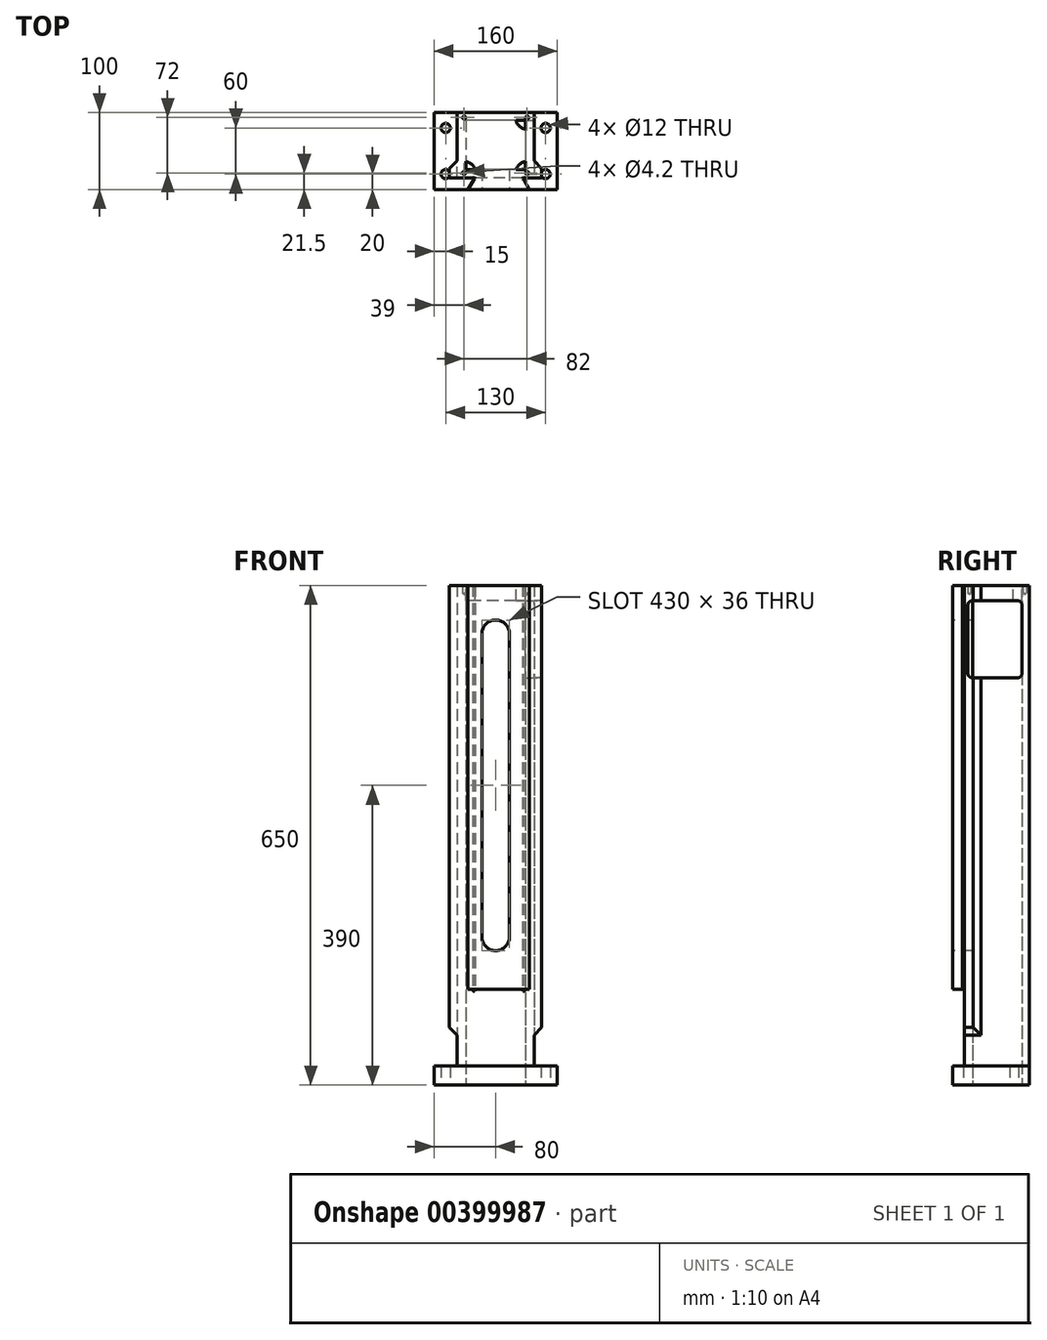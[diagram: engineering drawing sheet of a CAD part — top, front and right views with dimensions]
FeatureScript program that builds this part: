
annotation { "Feature Type Name" : "Feature", "Feature Type Description" : "" }
export const myFeature = defineFeature(function(context is Context, id is Id, definition is map)
    precondition{}
    {
        {
            var Q0;
            Q0=qCreatedBy(makeId("Top.planeOp"),FACE);
            var sketch = newSketch(context, id + "F0", { "sketchPlane" : qUnion([Q0])});
            skLineSegment(sketch, "E0.bottom", {"start": v(80, 50) * mm, "end": v(-80, 50) * mm});
            skLineSegment(sketch, "E0.top", {"start": v(80, -50) * mm, "end": v(-80, -50) * mm});
            skLineSegment(sketch, "E0.left", {"start": v(80, 50) * mm, "end": v(80, -50) * mm});
            skLineSegment(sketch, "E0.right", {"start": v(-80, 50) * mm, "end": v(-80, -50) * mm});
            skLineSegment(sketch, "E1", {"start": v(-80, 0) * mm, "end": v(80, 0) * mm, "construction": true});
            skLineSegment(sketch, "E2", {"start": v(0, 50) * mm, "end": v(0, -50) * mm, "construction": true});
            skCircle(sketch, "E3", {"center": v(-65, 30) * mm, "radius": 6 * mm});
            skCircle(sketch, "E4", {"center": v(-65, -30) * mm, "radius": 6 * mm});
            skCircle(sketch, "E5.MirrorC", {"center": v(65, 30) * mm, "radius": 6 * mm});
            skCircle(sketch, "E6.MirrorC", {"center": v(65, -30) * mm, "radius": 6 * mm});
            skLineSegment(sketch, "E7.bottom", {"start": v(39, 40) * mm, "end": v(-39, 40) * mm});
            skLineSegment(sketch, "E7.top", {"start": v(39, -24) * mm, "end": v(-39, -24) * mm});
            skLineSegment(sketch, "E7.left", {"start": v(39, 40) * mm, "end": v(39, -24) * mm});
            skLineSegment(sketch, "E7.right", {"start": v(-39, 40) * mm, "end": v(-39, -24) * mm});
            skPoint(sketch, "E7.middle", {"position": v(0, 0) * mm});
            skPoint(sketch, "E8", {"position": v(0, -24) * mm});
            skSolve(sketch);
        }
        {
            var Q0;
            Q0=qSketchRegion(id+"F0",true);
            extrude(context, id + "F1", {"entities" : qUnion([Q0]), "depth" : 25 * mm});
        }
        {
            var Q0;
            Q0=makeQuery(id+"F1.opExtrude","CAP_FACE",FACE,{"disambiguationData":[OSD([sQuery(id+"F0.wireOp",EDGE,"E0.bottom"),sQuery(id+"F0.wireOp",EDGE,"E0.top"),sQuery(id+"F0.wireOp",EDGE,"E0.left"),sQuery(id+"F0.wireOp",EDGE,"E0.right")])],"isStart":false});
            var sketch = newSketch(context, id + "F2", { "sketchPlane" : qUnion([Q0])});
            skLineSegment(sketch, "E9", {"start": v(-50, 50) * mm, "end": v(50, 50) * mm});
            skLineSegment(sketch, "E10", {"start": v(50, 50) * mm, "end": v(50, -13) * mm});
            skLineSegment(sketch, "E11", {"start": v(50, -13) * mm, "end": v(60, -23) * mm});
            skLineSegment(sketch, "E12", {"start": v(60, -23) * mm, "end": v(60, -35) * mm});
            skLineSegment(sketch, "E13", {"start": v(60, -35) * mm, "end": v(35.34, -35) * mm});
            skLineSegment(sketch, "E14", {"start": v(35.34, -35) * mm, "end": v(44, -50) * mm});
            skLineSegment(sketch, "E15", {"start": v(44, -50) * mm, "end": v(-36, -50) * mm});
            skLineSegment(sketch, "E16", {"start": v(-36, -50) * mm, "end": v(-27.34, -35) * mm});
            skLineSegment(sketch, "E17", {"start": v(-27.34, -35) * mm, "end": v(-60, -35) * mm});
            skLineSegment(sketch, "E18", {"start": v(-60, -35) * mm, "end": v(-60, -23) * mm});
            skLineSegment(sketch, "E19", {"start": v(-60, -23) * mm, "end": v(-50, -13) * mm});
            skLineSegment(sketch, "E20", {"start": v(-50, -13) * mm, "end": v(-50, 50) * mm});
            skLineSegment(sketch, "E21.bottom", {"start": v(-39, 40) * mm, "end": v(39, 40) * mm});
            skLineSegment(sketch, "E21.top", {"start": v(-39, -24) * mm, "end": v(39, -24) * mm});
            skLineSegment(sketch, "E21.left", {"start": v(-39, 40) * mm, "end": v(-39, -24) * mm});
            skLineSegment(sketch, "E21.right", {"start": v(39, 40) * mm, "end": v(39, -24) * mm});
            skLineSegment(sketch, "E22", {"start": v(0, 40) * mm, "end": v(0, -24) * mm, "construction": true});
            skSolve(sketch);
        }
        {
            var Q0;
            Q0=qSketchRegion(id+"F2",true);
            extrude(context, id + "F3", {"entities" : qUnion([Q0]), "operationType" : NewBodyOperationType.ADD, "depth" : 625 * mm});
        }
        {
            var Q0;
            Q0=makeQuery(id+"F3.opExtrude","SWEPT_FACE",FACE,{"disambiguationData":[OSD([sQuery(id+"F2.wireOp",EDGE,"E15")])]});
            var sketch = newSketch(context, id + "F4", { "sketchPlane" : qUnion([Q0])});
            skLineSegment(sketch, "E23.left", {"start": v(18, 193) * mm, "end": v(18, 587) * mm});
            skLineSegment(sketch, "E23.right", {"start": v(-18, 193) * mm, "end": v(-18, 587) * mm});
            skPoint(sketch, "E23.middle", {"position": v(0, 390) * mm});
            skArc(sketch, "E24", {"start": v(-18, 587) * mm, "mid": v(0, 605) * mm, "end": v(18, 587) * mm});
            skArc(sketch, "E25", {"start": v(-18, 193) * mm, "mid": v(0, 175) * mm, "end": v(18, 193) * mm});
            skSolve(sketch);
        }
        {
            var Q0;
            Q0=makeQuery(id+"F4.imprint","IMPRINT",FACE,{"disambiguationData":[TD([[makeQuery(id+"F4.imprint","IMPRINT",EDGE,{"derivedFrom":sQuery(id+"F4.wireOp",EDGE,"E23.left")}),1.0]])]});
            extrude(context, id + "F5", {"entities" : qUnion([Q0]), "operationType" : NewBodyOperationType.REMOVE, "endBound" : BoundingType.UP_TO_NEXT, "oppositeDirection" : true, "depth" : 25 * mm});
        }
        {
            var Q0;
            Q0=makeQuery(id+"F3.boolean.opBoolean","MERGE",FACE,{"derivedFrom":[makeQuery(id+"F1.opExtrude","SWEPT_FACE",FACE,{"disambiguationData":[OSD([sQuery(id+"F0.wireOp",EDGE,"E0.top")])]}),makeQuery(id+"F3.opExtrude","SWEPT_FACE",FACE,{"disambiguationData":[OSD([sQuery(id+"F2.wireOp",EDGE,"E15")])]})]});
            var sketch = newSketch(context, id + "F6", { "sketchPlane" : qUnion([Q0])});
            skLineSegment(sketch, "E26.bottom", {"start": v(-36, 25) * mm, "end": v(44, 25) * mm});
            skLineSegment(sketch, "E26.top", {"start": v(-36, 125) * mm, "end": v(44, 125) * mm});
            skLineSegment(sketch, "E26.left", {"start": v(-36, 25) * mm, "end": v(-36, 125) * mm});
            skLineSegment(sketch, "E26.right", {"start": v(44, 25) * mm, "end": v(44, 125) * mm});
            skSolve(sketch);
        }
        {
            var Q0;
            Q0=qSketchRegion(id+"F6",true);
            var Q1;
            Q1=makeQuery(id+"F3.opExtrude","SWEPT_FACE",FACE,{"disambiguationData":[OSD([sQuery(id+"F2.wireOp",EDGE,"E17")])]});
            extrude(context, id + "F7", {"entities" : qUnion([Q0]), "operationType" : NewBodyOperationType.REMOVE, "endBound" : BoundingType.UP_TO_SURFACE, "oppositeDirection" : true, "endBoundEntityFace" : qUnion([Q1]), "depth" : 25 * mm});
        }
        {
            var Q0;
            {var subQ0=sQuery(id+"F2.wireOp",EDGE,"E17");Q0=makeQuery(id+"F7.boolean.opBoolean","MERGE",FACE,{"derivedFrom":[makeQuery(id+"F3.opExtrude","SWEPT_FACE",FACE,{"disambiguationData":[OSD([sQuery(id+"F2.wireOp",EDGE,"E13")])]}),makeQuery(id+"F3.opExtrude","SWEPT_FACE",FACE,{"disambiguationData":[OSD([subQ0])]}),makeQuery(id+"F7.opExtrude","CAP_FACE",FACE,{"disambiguationData":[OSD([subQ0])],"isStart":false})]});}
            var sketch = newSketch(context, id + "F8", { "sketchPlane" : qUnion([Q0])});
            skLineSegment(sketch, "E27", {"start": v(-60, 25) * mm, "end": v(-50, 25) * mm});
            skLineSegment(sketch, "E28", {"start": v(-50, 25) * mm, "end": v(-50, 65) * mm});
            skLineSegment(sketch, "E29", {"start": v(-50, 65) * mm, "end": v(-60, 75) * mm});
            skLineSegment(sketch, "E30", {"start": v(-60, 75) * mm, "end": v(-60, 25) * mm});
            skLineSegment(sketch, "E31", {"start": v(0, 25) * mm, "end": v(0, 75) * mm, "construction": true});
            skLineSegment(sketch, "E32.MirrorCS", {"start": v(50, 25) * mm, "end": v(50, 65) * mm});
            skLineSegment(sketch, "E33.MirrorCS", {"start": v(60, 25) * mm, "end": v(50, 25) * mm});
            skLineSegment(sketch, "E34.MirrorCS", {"start": v(60, 75) * mm, "end": v(60, 25) * mm});
            skLineSegment(sketch, "E35.MirrorCS", {"start": v(50, 65) * mm, "end": v(60, 75) * mm});
            skSolve(sketch);
        }
        {
            var Q0;
            Q0=qSketchRegion(id+"F8",true);
            var Q1;
            Q1=makeQuery(id+"F3.opExtrude","CAP_VERTEX",VERTEX,{"disambiguationData":[OSD([sQuery(id+"F2.wireOp",EDGE,"E19"),sQuery(id+"F2.wireOp",EDGE,"E20")])],"isStart":true});
            extrude(context, id + "F9", {"entities" : qUnion([Q0]), "operationType" : NewBodyOperationType.REMOVE, "endBound" : BoundingType.UP_TO_VERTEX, "oppositeDirection" : true, "endBoundEntityVertex" : qUnion([Q1]), "depth" : 25 * mm});
        }
        {
            var Q0;
            Q0=makeQuery(id+"F3.opExtrude","CAP_FACE",FACE,{"disambiguationData":[OSD([sQuery(id+"F2.wireOp",EDGE,"E9"),sQuery(id+"F2.wireOp",EDGE,"E10"),sQuery(id+"F2.wireOp",EDGE,"E11"),sQuery(id+"F2.wireOp",EDGE,"E12"),sQuery(id+"F2.wireOp",EDGE,"E13"),sQuery(id+"F2.wireOp",EDGE,"E14"),sQuery(id+"F2.wireOp",EDGE,"E15"),sQuery(id+"F2.wireOp",EDGE,"E16"),sQuery(id+"F2.wireOp",EDGE,"E17"),sQuery(id+"F2.wireOp",EDGE,"E18"),sQuery(id+"F2.wireOp",EDGE,"E19"),sQuery(id+"F2.wireOp",EDGE,"E20"),sQuery(id+"F2.wireOp",EDGE,"E21.bottom"),sQuery(id+"F2.wireOp",EDGE,"E21.top"),sQuery(id+"F2.wireOp",EDGE,"E21.left"),sQuery(id+"F2.wireOp",EDGE,"E21.right")])],"isStart":false});
            var sketch = newSketch(context, id + "F10", { "sketchPlane" : qUnion([Q0])});
            skPoint(sketch, "E36", {"position": v(-41, 43.5) * mm});
            skPoint(sketch, "E37", {"position": v(-41, -28.5) * mm});
            skPoint(sketch, "E38", {"position": v(41, -28.5) * mm});
            skPoint(sketch, "E39", {"position": v(41, 43.5) * mm});
            skLineSegment(sketch, "E40", {"start": v(0, 50) * mm, "end": v(0, -35) * mm, "construction": true});
            skLineSegment(sketch, "E41", {"start": v(0, 7.5) * mm, "end": v(-50, 7.5) * mm, "construction": true});
            skSolve(sketch);
        }
        {
            var Q0;
            Q0=sQuery(id+"F10.wireOp",VERTEX,"E36");
            var Q1;
            Q1=sQuery(id+"F10.wireOp",VERTEX,"E39");
            var Q2;
            Q2=sQuery(id+"F10.wireOp",VERTEX,"E38");
            var Q3;
            Q3=sQuery(id+"F10.wireOp",VERTEX,"E37");
            var Q4;
            Q4=makeQuery(id+"F1.opExtrude","SWEPT_BODY",BODY,{"disambiguationData":[OSD([sQuery(id+"F0.wireOp",EDGE,"E0.bottom"),sQuery(id+"F0.wireOp",EDGE,"E0.top"),sQuery(id+"F0.wireOp",EDGE,"E0.left"),sQuery(id+"F0.wireOp",EDGE,"E0.right"),sQuery(id+"F0.wireOp",EDGE,"E3"),sQuery(id+"F0.wireOp",EDGE,"E4"),sQuery(id+"F0.wireOp",EDGE,"E5.MirrorC"),sQuery(id+"F0.wireOp",EDGE,"E6.MirrorC")])]});
            hole(context, id + "F11", {"style" : HoleStyle.SIMPLE, "endStyle" : HoleEndStyle.BLIND, "standardTappedOrClearance" : lookupTablePath({ "standard" : "ISO", "engagement" : "75%", "pitch" : "0.8 mm", "size" : "M5", "type" : "Tapped" }), "standardBlindInLast" : lookupTablePath({ "standard" : "ISO", "engagement" : "75%", "pitch" : "0.8 mm", "size" : "M5", "type" : "Tapped" }), "holeDiameter" : 4.2 * mm, "showTappedDepth" : true, "holeDepth" : 10.4 * mm, "isTappedThrough" : true, "tappedDepth" : 8 * mm, "tapClearance" : 3, "locations" : qUnion([Q0, Q1, Q2, Q3]), "scope" : qUnion([Q4]), "majorDiameter" : 5 * mm, "startStyle" : HoleStartStyle.SKETCH});
        }
        {
            var Q0;
            Q0=makeQuery(id+"F3.opExtrude","CAP_FACE",FACE,{"disambiguationData":[OSD([sQuery(id+"F2.wireOp",EDGE,"E9"),sQuery(id+"F2.wireOp",EDGE,"E10"),sQuery(id+"F2.wireOp",EDGE,"E11"),sQuery(id+"F2.wireOp",EDGE,"E12"),sQuery(id+"F2.wireOp",EDGE,"E13"),sQuery(id+"F2.wireOp",EDGE,"E14"),sQuery(id+"F2.wireOp",EDGE,"E15"),sQuery(id+"F2.wireOp",EDGE,"E16"),sQuery(id+"F2.wireOp",EDGE,"E17"),sQuery(id+"F2.wireOp",EDGE,"E18"),sQuery(id+"F2.wireOp",EDGE,"E19"),sQuery(id+"F2.wireOp",EDGE,"E20"),sQuery(id+"F2.wireOp",EDGE,"E21.bottom"),sQuery(id+"F2.wireOp",EDGE,"E21.top"),sQuery(id+"F2.wireOp",EDGE,"E21.left"),sQuery(id+"F2.wireOp",EDGE,"E21.right")])],"isStart":false});
            var sketch = newSketch(context, id + "F12", { "sketchPlane" : qUnion([Q0])});
            skArc(sketch, "E42", {"start": v(-39, -13.63) * mm, "mid": v(-31.34, -17.03) * mm, "end": v(-26.7, -24) * mm});
            skArc(sketch, "E43", {"start": v(-39, 28.63) * mm, "mid": v(-30.95, 32.37) * mm, "end": v(-26.41, 40) * mm});
            skArc(sketch, "E44", {"start": v(39, 28.63) * mm, "mid": v(30.95, 32.37) * mm, "end": v(26.41, 40) * mm});
            skArc(sketch, "E45", {"start": v(26.7, -24) * mm, "mid": v(31.34, -17.03) * mm, "end": v(39, -13.63) * mm});
            skSolve(sketch);
        }
        {
            var Q0;
            {var subQ0=sQuery(id+"F12.wireOp",EDGE,"E43");Q0=makeQuery(id+"F12.imprint","IMPRINT",FACE,{"disambiguationData":[TD([[makeQuery(id+"F12.imprint","IMPRINT",EDGE,{"derivedFrom":subQ0}),1.0]])]});}
            var Q1;
            {var subQ0=sQuery(id+"F12.wireOp",EDGE,"E44");Q1=makeQuery(id+"F12.imprint","IMPRINT",FACE,{"disambiguationData":[TD([[makeQuery(id+"F12.imprint","IMPRINT",EDGE,{"derivedFrom":subQ0}),-1.0]])]});}
            var Q2;
            {var subQ0=sQuery(id+"F12.wireOp",EDGE,"E42");Q2=makeQuery(id+"F12.imprint","IMPRINT",FACE,{"disambiguationData":[TD([[makeQuery(id+"F12.imprint","IMPRINT",EDGE,{"derivedFrom":subQ0}),-1.0]])]});}
            var Q3;
            {var subQ0=sQuery(id+"F12.wireOp",EDGE,"E45");Q3=makeQuery(id+"F12.imprint","IMPRINT",FACE,{"disambiguationData":[TD([[makeQuery(id+"F12.imprint","IMPRINT",EDGE,{"derivedFrom":subQ0}),-1.0]])]});}
            extrude(context, id + "F13", {"entities" : qUnion([Q0, Q1, Q2, Q3]), "operationType" : NewBodyOperationType.ADD, "oppositeDirection" : true, "depth" : 20 * mm});
        }
        {
            var Q0;
            Q0=makeQuery(id+"F3.opExtrude","SWEPT_FACE",FACE,{"disambiguationData":[OSD([sQuery(id+"F2.wireOp",EDGE,"E12")])]});
            var sketch = newSketch(context, id + "F14", { "sketchPlane" : qUnion([Q0])});
            skLineSegment(sketch, "E46.bottom", {"start": v(-25, 630) * mm, "end": v(35, 630) * mm});
            skLineSegment(sketch, "E46.top", {"start": v(-25, 530) * mm, "end": v(35, 530) * mm});
            skLineSegment(sketch, "E46.left", {"start": v(-30, 625) * mm, "end": v(-30, 535) * mm});
            skLineSegment(sketch, "E46.right", {"start": v(40, 625) * mm, "end": v(40, 535) * mm});
            skPoint(sketch, "E47.visualSharp", {"position": v(-30, 630) * mm});
            skArc(sketch, "E47.filletArc", {"start": v(-25, 630) * mm, "mid": v(-28.54, 628.54) * mm, "end": v(-30, 625) * mm});
            skPoint(sketch, "E48.visualSharp", {"position": v(40, 630) * mm});
            skArc(sketch, "E48.filletArc", {"start": v(40, 625) * mm, "mid": v(38.54, 628.54) * mm, "end": v(35, 630) * mm});
            skPoint(sketch, "E49.visualSharp", {"position": v(40, 530) * mm});
            skArc(sketch, "E49.filletArc", {"start": v(35, 530) * mm, "mid": v(38.54, 531.46) * mm, "end": v(40, 535) * mm});
            skPoint(sketch, "E50.visualSharp", {"position": v(-30, 530) * mm});
            skArc(sketch, "E50.filletArc", {"start": v(-30, 535) * mm, "mid": v(-28.54, 531.46) * mm, "end": v(-25, 530) * mm});
            skSolve(sketch);
        }
        {
            var Q0;
            Q0=makeQuery(id+"F14.imprint","IMPRINT",FACE,{"disambiguationData":[TD([[makeQuery(id+"F14.imprint","IMPRINT",EDGE,{"derivedFrom":sQuery(id+"F14.wireOp",EDGE,"E46.right")}),-1.0]])]});
            var Q1;
            Q1=makeQuery(id+"F14.imprint","IMPRINT",FACE,{"disambiguationData":[TD([[makeQuery(id+"F14.imprint","IMPRINT",EDGE,{"derivedFrom":sQuery(id+"F14.wireOp",EDGE,"E46.left")}),1.0]])]});
            var Q2;
            Q2=makeQuery(id+"F3.opExtrude","SWEPT_FACE",FACE,{"disambiguationData":[OSD([sQuery(id+"F2.wireOp",EDGE,"E21.right")])]});
            extrude(context, id + "F15", {"entities" : qUnion([Q0, Q1]), "operationType" : NewBodyOperationType.REMOVE, "endBound" : BoundingType.UP_TO_SURFACE, "oppositeDirection" : true, "endBoundEntityFace" : qUnion([Q2]), "depth" : 25 * mm});
        }
        {
            var Q0;
            Q0=makeQuery(id+"F7.boolean.opBoolean","COPY",FACE,{"derivedFrom":makeQuery(id+"F7.opExtrude","SWEPT_FACE",FACE,{"disambiguationData":[OSD([sQuery(id+"F6.wireOp",EDGE,"E26.top")])]})});
            var sketch = newSketch(context, id + "F16", { "sketchPlane" : qUnion([Q0])});
            skLineSegment(sketch, "E51", {"start": v(34.71, 36.08) * mm, "end": v(36.59, 37.17) * mm});
            skLineSegment(sketch, "E52", {"start": v(36.59, 37.17) * mm, "end": v(37.84, 35) * mm});
            skLineSegment(sketch, "E53", {"start": v(37.84, 35) * mm, "end": v(35.96, 33.92) * mm});
            skLineSegment(sketch, "E54", {"start": v(35.96, 33.92) * mm, "end": v(34.71, 36.08) * mm});
            skLineSegment(sketch, "E55", {"start": v(35.34, 35) * mm, "end": v(37.21, 36.08) * mm, "construction": true});
            skLineSegment(sketch, "E56", {"start": v(4, 35) * mm, "end": v(4, 50) * mm, "construction": true});
            skLineSegment(sketch, "E57.MirrorCS", {"start": v(-26.71, 36.08) * mm, "end": v(-28.59, 37.17) * mm});
            skLineSegment(sketch, "E58.MirrorCS", {"start": v(-28.59, 37.17) * mm, "end": v(-29.84, 35) * mm});
            skLineSegment(sketch, "E59.MirrorCS", {"start": v(-29.84, 35) * mm, "end": v(-27.96, 33.92) * mm});
            skLineSegment(sketch, "E60.MirrorCS", {"start": v(-27.96, 33.92) * mm, "end": v(-26.71, 36.08) * mm});
            skSolve(sketch);
        }
        {
            var Q0;
            Q0=qSketchRegion(id+"F16",true);
            var Q1;
            {var subQ0=sQuery(id+"F2.wireOp",EDGE,"E21.right");var subQ1=sQuery(id+"F2.wireOp",EDGE,"E21.top");var subQ2=sQuery(id+"F2.wireOp",EDGE,"E21.bottom");var subQ3=sQuery(id+"F2.wireOp",EDGE,"E21.left");Q1=makeQuery(id+"F13.boolean.opBoolean","MERGE",FACE,{"derivedFrom":[makeQuery(id+"F3.opExtrude","CAP_FACE",FACE,{"disambiguationData":[OSD([sQuery(id+"F2.wireOp",EDGE,"E9"),sQuery(id+"F2.wireOp",EDGE,"E10"),sQuery(id+"F2.wireOp",EDGE,"E11"),sQuery(id+"F2.wireOp",EDGE,"E12"),sQuery(id+"F2.wireOp",EDGE,"E13"),sQuery(id+"F2.wireOp",EDGE,"E14"),sQuery(id+"F2.wireOp",EDGE,"E15"),sQuery(id+"F2.wireOp",EDGE,"E16"),sQuery(id+"F2.wireOp",EDGE,"E17"),sQuery(id+"F2.wireOp",EDGE,"E18"),sQuery(id+"F2.wireOp",EDGE,"E19"),sQuery(id+"F2.wireOp",EDGE,"E20"),subQ2,subQ1,subQ3,subQ0])],"isStart":false}),makeQuery(id+"F13.opExtrude","CAP_FACE",FACE,{"disambiguationData":[OSD([subQ1,subQ3,sQuery(id+"F12.wireOp",EDGE,"E42")])],"isStart":true}),makeQuery(id+"F13.opExtrude","CAP_FACE",FACE,{"disambiguationData":[OSD([subQ2,subQ3,sQuery(id+"F12.wireOp",EDGE,"E43")])],"isStart":true}),makeQuery(id+"F13.opExtrude","CAP_FACE",FACE,{"disambiguationData":[OSD([subQ2,subQ0,sQuery(id+"F12.wireOp",EDGE,"E44")])],"isStart":true}),makeQuery(id+"F13.opExtrude","CAP_FACE",FACE,{"disambiguationData":[OSD([subQ1,subQ0,sQuery(id+"F12.wireOp",EDGE,"E45")])],"isStart":true})]});}
            extrude(context, id + "F17", {"entities" : qUnion([Q0]), "operationType" : NewBodyOperationType.REMOVE, "endBound" : BoundingType.UP_TO_SURFACE, "oppositeDirection" : true, "endBoundEntityFace" : qUnion([Q1]), "depth" : 25 * mm, "hasSecondDirection" : true, "secondDirectionOppositeDirection" : false, "secondDirectionDepth" : 3 * mm});
        }
        {
            var Q0;
            Q0=makeQuery(id+"F17.boolean.opBoolean","COPY",EDGE,{"derivedFrom":makeQuery(id+"F17.opExtrude","CAP_EDGE",EDGE,{"disambiguationData":[OSD([sQuery(id+"F16.wireOp",EDGE,"E53")])],"isStart":true})});
            var Q1;
            Q1=makeQuery(id+"F17.boolean.opBoolean","COPY",EDGE,{"derivedFrom":makeQuery(id+"F17.opExtrude","CAP_EDGE",EDGE,{"disambiguationData":[OSD([sQuery(id+"F16.wireOp",EDGE,"E59.MirrorCS")])],"isStart":true})});
            fillet(context, id + "F18", {"entities" : qUnion([Q0, Q1]), "radius" : 1.25 * mm, "tangentPropagation" : true, "allowEdgeOverflow" : false});
        }
    });
